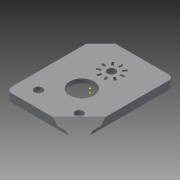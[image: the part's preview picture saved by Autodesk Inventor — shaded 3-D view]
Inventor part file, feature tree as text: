
AUTODESK INVENTOR PART (.ipt)
format: ipt  version: 2015 SP1 (Build 190203100, 203)  size: 228,864 bytes
history: native  units: mm
features: sketch x6, extrude x4, reference x4, other x2, projected_geometry x1
ambient origin geometry x8: Origin, YZ Plane, XZ Plane, XY Plane, X Axis, Y Axis, Z Axis, Center Point
bodies: Body1 (feature_tree)
feature tree (17):
  other  "Sólido1"
  sketch  "Boceto1"  dims[d0=2.5mm d1=0.0mm]
  extrude  "Extrusión1"  Depth=1.0mm
  sketch  "Boceto3"  dims[d9=9.0mm d10=1.5mm d11=0.0mm]
  other  "Labio1"
  extrude  "Extrusión2"  Depth=1.5mm TaperAngle=0.0deg
  sketch  "Boceto7"  dims[d41=80.0mm d43=360.0deg d45=90.0mm d47=360.0deg]
  extrude  "Extrusión4"  Depth=10.0mm TaperAngle=0.0deg
  extrude  "Extrusión5"  Depth=0.75mm
  sketch  "Boceto2"  dims[d2=1.0mm d3=1.0mm d4=0.0mm d5=0.0mm d6=0.0mm d7=0.0mm d8=12.5mm]
  reference  "Referencia1"
  reference  "Referencia2"
  sketch  "Boceto4"  dims[d16=10.0mm d17=0.0mm d36=10.0mm d37=0.0mm]
  reference  "Referencia3"
  reference  "Referencia4"
  sketch  "Boceto6"  dims[d38=3.0mm d39=0.75mm]
  projected_geometry  "Contorno proyectado2"
